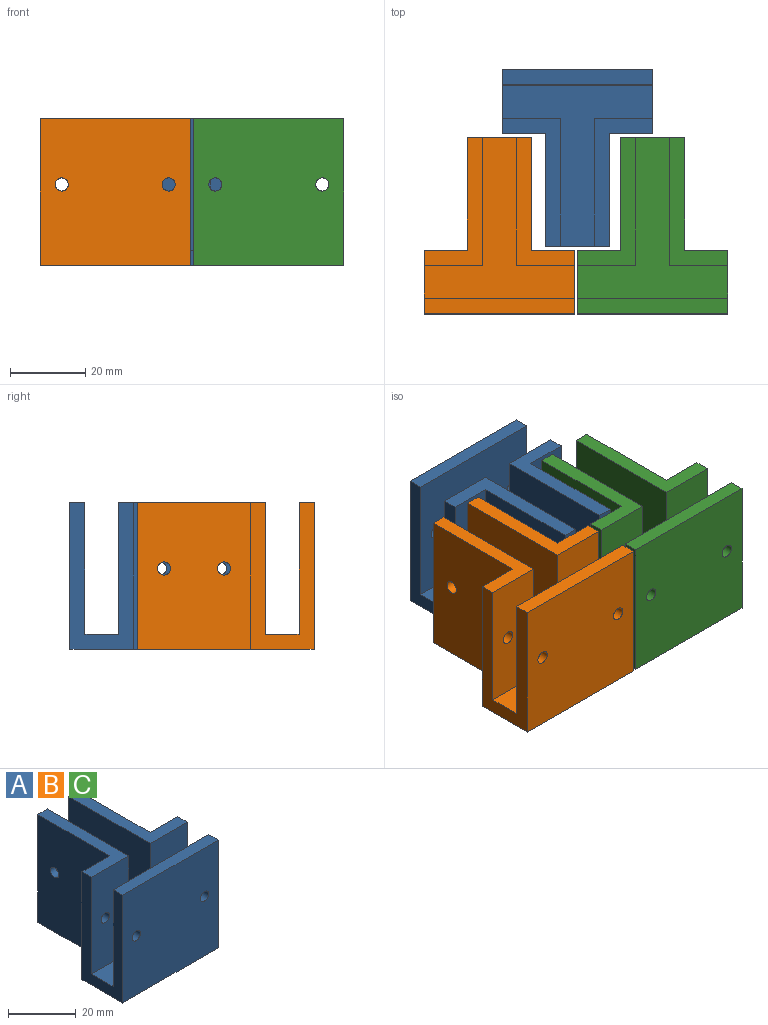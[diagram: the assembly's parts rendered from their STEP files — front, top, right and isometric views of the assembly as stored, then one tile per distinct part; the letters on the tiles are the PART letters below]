
ASSEMBLY  parts=3 mates=3
PART A: 26 faces, bbox 40x47x39 mm
  f0: plane 43x40mm, normal (0,0,1), area 666mm2, adj f1,f3,f6,f10,f12,f13,f15,f16
  f1: plane 39x17mm, normal (-1,0,0), area 348mm2, adj f0,f2,f8,f9,f10,f11,f12,f14
  f2: plane 40x39mm, normal (0,-1,0), area 1540.8mm2, adj f1,f3,f9,f11,f20,f21
  f3: plane 39x17mm, normal (1,0,0), area 348mm2, adj f0,f2,f4,f9,f10,f11,f16,f17
  f4: plane 39x11.5mm, normal (0,1,0), area 438.9mm2, adj f3,f5,f9,f17,f18
  f5: plane 39x30mm, normal (1,0,0), area 1150.8mm2, adj f4,f6,f9,f17,f22,f23
  f6: plane 39x17mm, normal (0,1,0), area 348mm2, adj f0,f5,f7,f9,f13,f14,f15,f17
  f7: plane 39x30mm, normal (-1,0,0), area 1150.8mm2, adj f6,f8,f9,f14,f24,f25
  f8: plane 39x11.5mm, normal (0,1,0), area 438.9mm2, adj f1,f7,f9,f14,f19
  f9: plane 47x40mm, normal (0,0,-1), area 1190mm2, adj f1,f2,f3,f4,f5,f6,f7,f8
  f10: plane 40x35mm, normal (0,1,0), area 1380.8mm2, adj f0,f1,f3,f11,f20,f21
  f11: plane 40x4mm, normal (0,0,1), area 160mm2, adj f1,f2,f3,f10
  f12: plane 35x15.5mm, normal (0,-1,0), area 532.9mm2, adj f0,f1,f13,f14,f19
  f13: plane 35x34mm, normal (1,0,0), area 1170.8mm2, adj f0,f6,f12,f14,f24,f25
  f14: plane 34x15.5mm, normal (0,0,1), area 182mm2, adj f1,f6,f7,f8,f12,f13
  f15: plane 35x34mm, normal (-1,0,0), area 1170.8mm2, adj f0,f6,f16,f17,f22,f23
  f16: plane 35x15.5mm, normal (0,-1,0), area 532.9mm2, adj f0,f3,f15,f17,f18
  f17: plane 34x15.5mm, normal (0,0,1), area 182mm2, adj f3,f4,f5,f6,f15,f16
  f18: cylinder r=1.75mm len=4mm, axis (0,1,0), area 44mm2, adj f4,f16
  f19: cylinder r=1.75mm len=4mm, axis (0,1,0), area 44mm2, adj f8,f12
  f20: cylinder r=1.75mm len=4mm, axis (0,1,0), area 44mm2, adj f2,f10
  f21: cylinder r=1.75mm len=4mm, axis (0,1,0), area 44mm2, adj f2,f10
  f22: cylinder r=1.75mm len=4mm, axis (1,0,0), area 44mm2, adj f5,f15
  f23: cylinder r=1.75mm len=4mm, axis (1,0,0), area 44mm2, adj f5,f15
  f24: cylinder r=1.75mm len=4mm, axis (1,0,0), area 44mm2, adj f7,f13
  f25: cylinder r=1.75mm len=4mm, axis (1,0,0), area 44mm2, adj f7,f13
PART B: same geometry as A
PART C: same geometry as A
PLACE A rot(axis=(0,0,1),180deg) t=(-56.79,40.86,13.78)mm
PLACE B t=(-77.64,-24.21,13.78)mm
PLACE C t=(-36.69,-24.21,13.78)mm
MATE planar B.f2 <-> C.f2  axis (0,-1,0) through (-77.64,-24.21,33.26)mm
MATE planar A.f9 <-> C.f9  axis (0,0,-1) through (-56.79,22.28,13.78)mm
MATE planar C.f9 <-> B.f9  axis (0,0,-1) through (-36.69,-5.64,13.78)mm
